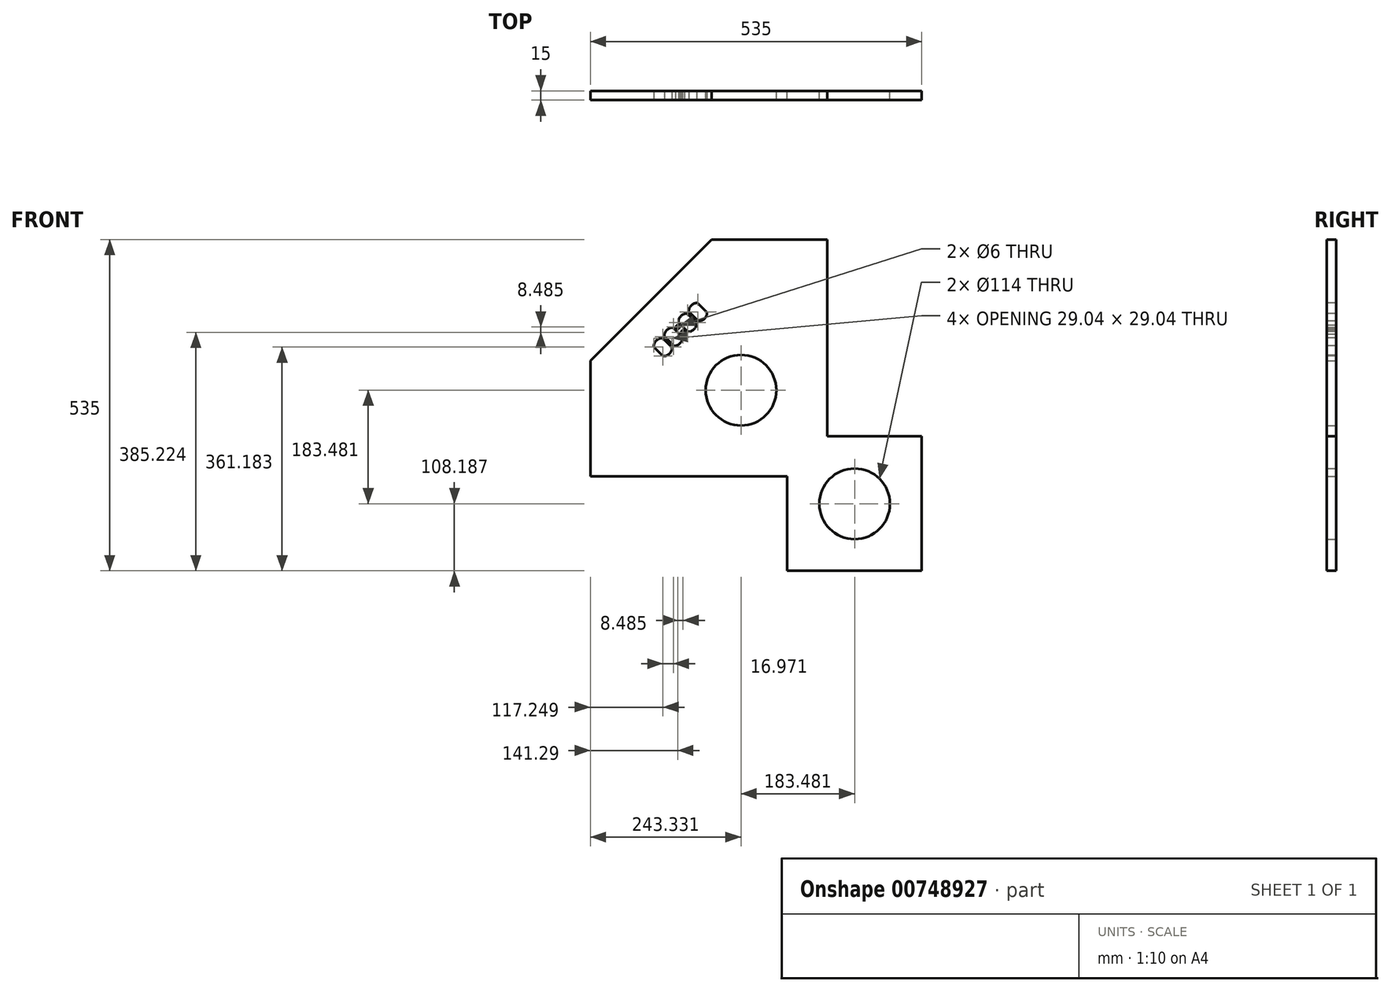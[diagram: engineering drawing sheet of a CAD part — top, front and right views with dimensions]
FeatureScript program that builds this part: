
annotation { "Feature Type Name" : "Feature", "Feature Type Description" : "" }
export const myFeature = defineFeature(function(context is Context, id is Id, definition is map)
    precondition{}
    {
        {
            var Q0;
            Q0=qCreatedBy(makeId("Front.planeOp"),FACE);
            var sketch = newSketch(context, id + "F0", { "sketchPlane" : qUnion([Q0])});
            skPoint(sketch, "E0.middle", {"position": v(0, 0) * mm});
            skLineSegment(sketch, "E1.0", {"start": v(-267.5, 71.9) * mm, "end": v(-71.9, 267.5) * mm});
            skLineSegment(sketch, "E1.1", {"start": v(115, 267.5) * mm, "end": v(-71.9, 267.5) * mm});
            skLineSegment(sketch, "E1.2", {"start": v(-267.5, -115) * mm, "end": v(-267.5, 71.9) * mm});
            skLineSegment(sketch, "E1.3", {"start": v(50, -267.5) * mm, "end": v(267.5, -267.5) * mm});
            skLineSegment(sketch, "E1.4", {"start": v(267.5, -50) * mm, "end": v(267.5, -267.5) * mm});
            skLineSegment(sketch, "E2", {"start": v(267.5, -267.5) * mm, "end": v(50, -267.5) * mm});
            skLineSegment(sketch, "E3", {"start": v(50, -267.5) * mm, "end": v(50, -260) * mm});
            skLineSegment(sketch, "E4.bottom", {"start": v(50, -260) * mm, "end": v(35, -260) * mm});
            skLineSegment(sketch, "E4.left", {"start": v(50, -260) * mm, "end": v(50, -130) * mm});
            skLineSegment(sketch, "E5.top", {"start": v(-260, -115) * mm, "end": v(35, -115) * mm});
            skLineSegment(sketch, "E6.trimOffspring", {"start": v(50, -130) * mm, "end": v(53, -130) * mm});
            skLineSegment(sketch, "E7.trimOffspring", {"start": v(50, -115) * mm, "end": v(53, -115) * mm});
            skLineSegment(sketch, "E8.trimOffspring", {"start": v(50, -115) * mm, "end": v(50, -112) * mm});
            skLineSegment(sketch, "E9.trimOffspring", {"start": v(35, -115) * mm, "end": v(35, -112) * mm});
            skLineSegment(sketch, "E10", {"start": v(-169.7, 169.7) * mm, "end": v(91.5, -91.5) * mm, "construction": true});
            skLineSegment(sketch, "E11.MirrorCS", {"start": v(115, -50) * mm, "end": v(112, -50) * mm});
            skLineSegment(sketch, "E12.MirrorCS", {"start": v(267.5, -50) * mm, "end": v(260, -50) * mm});
            skLineSegment(sketch, "E13.MirrorCS", {"start": v(130, -50) * mm, "end": v(130, -53) * mm});
            skLineSegment(sketch, "E14.MirrorCS", {"start": v(115, -50) * mm, "end": v(115, -53) * mm});
            skLineSegment(sketch, "E15.MirrorCS", {"start": v(115, -35) * mm, "end": v(112, -35) * mm});
            skLineSegment(sketch, "E16.MirrorCS", {"start": v(260, -50) * mm, "end": v(130, -50) * mm});
            skLineSegment(sketch, "E17.MirrorCS", {"start": v(115, 260) * mm, "end": v(115, -35) * mm});
            skLineSegment(sketch, "E18", {"start": v(-260, -115) * mm, "end": v(-267.5, -115) * mm});
            skLineSegment(sketch, "E19", {"start": v(115, 260) * mm, "end": v(115, 267.5) * mm});
            skCircle(sketch, "E20", {"center": v(159.31, -159.31) * mm, "radius": 57 * mm});
            skLineSegment(sketch, "E21", {"start": v(-169.7, 169.7) * mm, "end": v(-17.67, 17.67) * mm});
            skCircle(sketch, "E22", {"center": v(-24.17, 24.17) * mm, "radius": 57 * mm});
            skCircle(sketch, "E23", {"center": v(-126.2, 126.2) * mm, "radius": 3 * mm});
            skCircle(sketch, "E24", {"center": v(-117.72, 117.72) * mm, "radius": 3 * mm});
            skLineSegment(sketch, "E25.left", {"start": v(-132.57, 124.09) * mm, "end": v(-119.85, 111.36) * mm});
            skLineSegment(sketch, "E26", {"start": v(-143.89, 121.26) * mm, "end": v(-122.67, 100.05) * mm, "construction": true});
            skEllipse(sketch, "E27", {"center": v(-139.64, 117.02) * mm, "majorRadius": 10 * mm, "minorRadius": 6 * mm, "majorAxis": v(-0.7, -0.7)});
            skEllipse(sketch, "E28.MirrorC", {"center": v(-126.92, 104.29) * mm, "majorRadius": 10 * mm, "minorRadius": 6 * mm, "majorAxis": v(-0.7, -0.7)});
            skEllipse(sketch, "E29.MirrorC", {"center": v(-139.64, 117.02) * mm, "majorRadius": 10 * mm, "minorRadius": 6 * mm, "majorAxis": v(-0.7, -0.7)});
            skLineSegment(sketch, "E30.MirrorCS", {"start": v(-146.72, 109.95) * mm, "end": v(-133.99, 97.22) * mm});
            skEllipse(sketch, "E31.MirrorC", {"center": v(-126.92, 104.29) * mm, "majorRadius": 10 * mm, "minorRadius": 6 * mm, "majorAxis": v(0.7, 0.7)});
            skLineSegment(sketch, "E32.MirrorCS", {"start": v(-167.93, 97.22) * mm, "end": v(-160.86, 104.29) * mm});
            skEllipse(sketch, "E33.MirrorC", {"center": v(-143.89, 87.32) * mm, "majorRadius": 10 * mm, "minorRadius": 6 * mm, "majorAxis": v(-0.7, -0.7)});
            skLineSegment(sketch, "E34.MirrorCS", {"start": v(-149.54, 107.12) * mm, "end": v(-136.82, 94.39) * mm});
            skEllipse(sketch, "E35.MirrorC", {"center": v(-156.62, 100.05) * mm, "majorRadius": 10 * mm, "minorRadius": 6 * mm, "majorAxis": v(0.7, 0.7)});
            skLineSegment(sketch, "E36.MirrorCS", {"start": v(-163.69, 92.98) * mm, "end": v(-150.96, 80.25) * mm});
            skEllipse(sketch, "E37.MirrorC", {"center": v(-143.89, 87.32) * mm, "majorRadius": 10 * mm, "minorRadius": 6 * mm, "majorAxis": v(0.7, 0.7)});
            skEllipse(sketch, "E38.MirrorC", {"center": v(-156.62, 100.05) * mm, "majorRadius": 10 * mm, "minorRadius": 6 * mm, "majorAxis": v(0.7, 0.7)});
            skEllipse(sketch, "E39.MirrorC", {"center": v(-100.05, 156.62) * mm, "majorRadius": 10 * mm, "minorRadius": 6 * mm, "majorAxis": v(-0.7, -0.7)});
            skLineSegment(sketch, "E40.MirrorCS", {"start": v(-92.98, 163.69) * mm, "end": v(-80.25, 150.96) * mm});
            skEllipse(sketch, "E41.MirrorC", {"center": v(-104.29, 126.92) * mm, "majorRadius": 10 * mm, "minorRadius": 6 * mm, "majorAxis": v(-0.7, -0.7)});
            skLineSegment(sketch, "E42.MirrorCS", {"start": v(-109.95, 146.72) * mm, "end": v(-97.22, 133.99) * mm});
            skLineSegment(sketch, "E43.MirrorCS", {"start": v(-124.09, 132.57) * mm, "end": v(-111.36, 119.85) * mm});
            skLineSegment(sketch, "E44.MirrorCS", {"start": v(-107.12, 149.54) * mm, "end": v(-94.39, 136.82) * mm});
            skEllipse(sketch, "E45.MirrorC", {"center": v(-87.32, 143.89) * mm, "majorRadius": 10 * mm, "minorRadius": 6 * mm, "majorAxis": v(-0.7, -0.7)});
            skEllipse(sketch, "E46.MirrorC", {"center": v(-117.02, 139.64) * mm, "majorRadius": 10 * mm, "minorRadius": 6 * mm, "majorAxis": v(0.7, 0.7)});
            skLineSegment(sketch, "E47.MirrorCS", {"start": v(-121.26, 143.89) * mm, "end": v(-100.05, 122.67) * mm, "construction": true});
            skEllipse(sketch, "E48.MirrorC", {"center": v(-87.32, 143.89) * mm, "majorRadius": 10 * mm, "minorRadius": 6 * mm, "majorAxis": v(0.7, 0.7)});
            skEllipse(sketch, "E49.MirrorC", {"center": v(-100.05, 156.62) * mm, "majorRadius": 10 * mm, "minorRadius": 6 * mm, "majorAxis": v(-0.7, -0.7)});
            skEllipse(sketch, "E50.MirrorC", {"center": v(-104.29, 126.92) * mm, "majorRadius": 10 * mm, "minorRadius": 6 * mm, "majorAxis": v(0.7, 0.7)});
            skEllipse(sketch, "E51.MirrorC", {"center": v(-117.02, 139.64) * mm, "majorRadius": 10 * mm, "minorRadius": 6 * mm, "majorAxis": v(0.7, 0.7)});
            skPoint(sketch, "E52.middle", {"position": v(-121.97, 121.97) * mm});
            skLineSegment(sketch, "E53.0", {"start": v(-278.8, -241.44) * mm, "end": v(-278.8, -241.44) * mm});
            skLineSegment(sketch, "E53.1", {"start": v(-117.72, 117.72) * mm, "end": v(-126.2, 126.2) * mm, "construction": true});
            skPoint(sketch, "E54.orphan", {"position": v(-150.96, 114.19) * mm});
            skPoint(sketch, "E55.orphan", {"position": v(-115.6, 107.12) * mm});
            skPoint(sketch, "E25.top.end.orphan", {"position": v(-129.75, 92.98) * mm});
            skPoint(sketch, "E56.orphan", {"position": v(-136.82, 128.33) * mm});
            skLineSegment(sketch, "E57", {"start": v(267.5, -267.5) * mm, "end": v(159.31, -159.31) * mm});
            skLineSegment(sketch, "E58.left", {"start": v(267.5, -267.5) * mm, "end": v(267.5, 267.5) * mm});
            skLineSegment(sketch, "E59", {"start": v(-17.67, 17.67) * mm, "end": v(115, 17.67) * mm});
            skLineSegment(sketch, "E60", {"start": v(-17.67, 17.67) * mm, "end": v(-17.67, -115) * mm});
            skLineSegment(sketch, "E61", {"start": v(-267.5, 71.9) * mm, "end": v(-267.5, 267.5) * mm, "construction": true});
            skLineSegment(sketch, "E62", {"start": v(-71.9, 267.5) * mm, "end": v(-267.5, 267.5) * mm, "construction": true});
            skLineSegment(sketch, "E63", {"start": v(35, -115) * mm, "end": v(50, -115) * mm});
            skLineSegment(sketch, "E64", {"start": v(50, -130) * mm, "end": v(50, -115) * mm});
            skLineSegment(sketch, "E65", {"start": v(115, -35) * mm, "end": v(115, -50) * mm});
            skLineSegment(sketch, "E66", {"start": v(130, -50) * mm, "end": v(115, -50) * mm});
            skLineSegment(sketch, "E67", {"start": v(50, -260) * mm, "end": v(260, -260) * mm});
            skLineSegment(sketch, "E68", {"start": v(260, -260) * mm, "end": v(260, -50) * mm});
            skLineSegment(sketch, "E69.0", {"start": v(-260, -115) * mm, "end": v(-260, 68.79) * mm});
            skLineSegment(sketch, "E69.1", {"start": v(-260, 68.79) * mm, "end": v(-68.79, 260) * mm});
            skLineSegment(sketch, "E69.2", {"start": v(115, 260) * mm, "end": v(-68.79, 260) * mm});
            skLineSegment(sketch, "E70", {"start": v(-139.64, 83.08) * mm, "end": v(-150.97, 71.75) * mm});
            skSolve(sketch);
        }
        {
            var Q0;
            Q0=qSketchRegion(id+"F0",true);
            extrude(context, id + "F1", {"entities" : qUnion([Q0]), "depth" : 15 * mm, "offsetDistance" : 25 * mm, "symmetric" : true});
        }
    });
